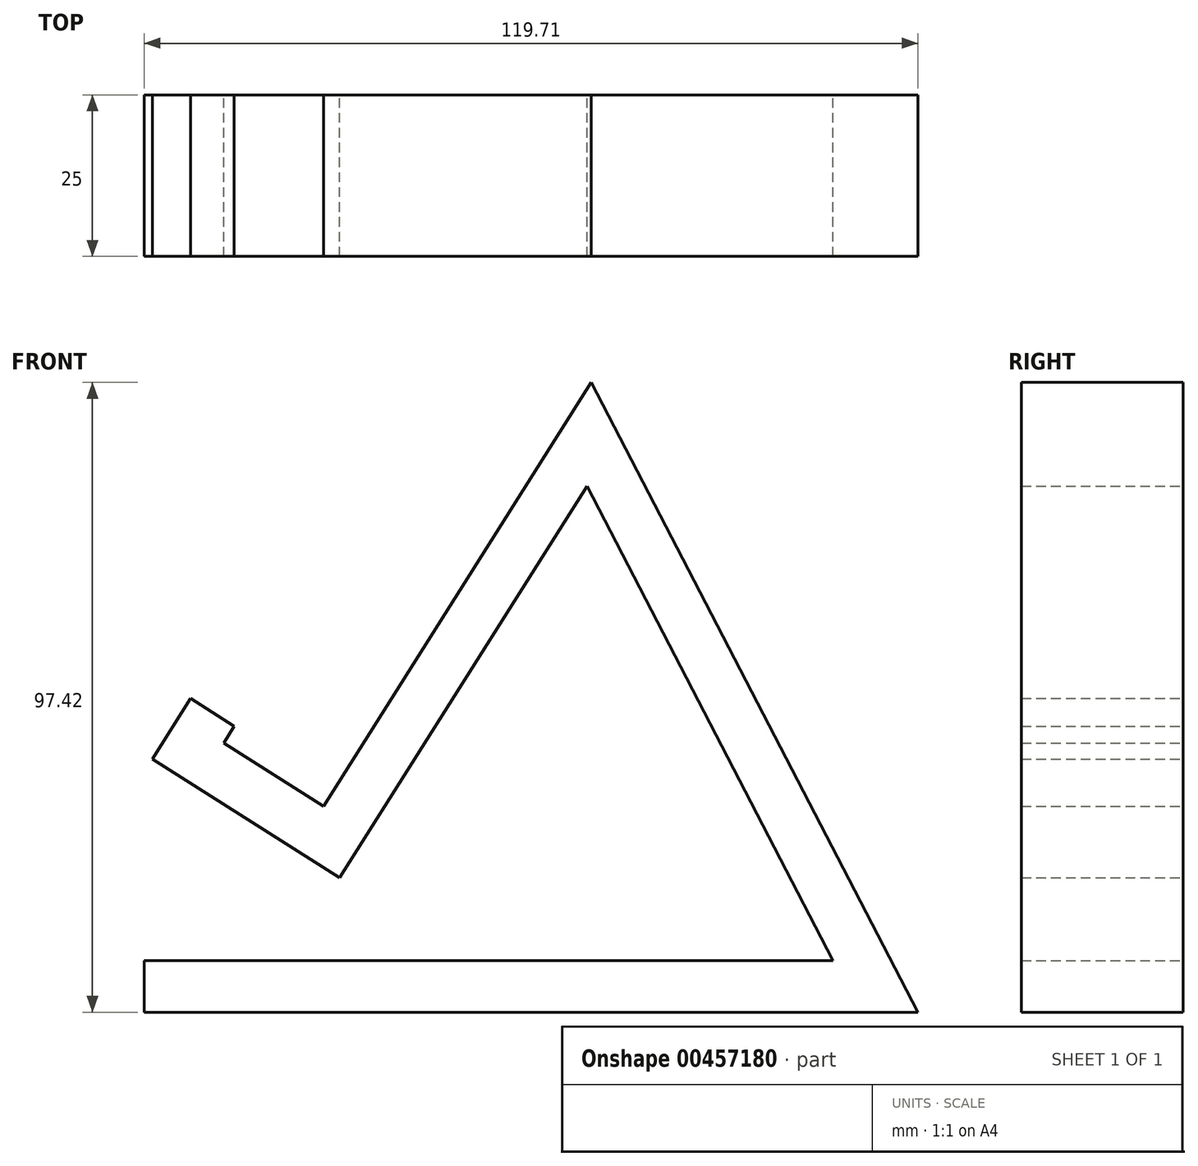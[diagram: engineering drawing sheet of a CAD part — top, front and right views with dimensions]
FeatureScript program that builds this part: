
annotation { "Feature Type Name" : "Feature", "Feature Type Description" : "" }
export const myFeature = defineFeature(function(context is Context, id is Id, definition is map)
    precondition{}
    {
        {
            var Q0;
            Q0=qCreatedBy(makeId("Front.planeOp"),FACE);
            var sketch = newSketch(context, id + "F0", { "sketchPlane" : qUnion([Q0])});
            skLineSegment(sketch, "E0", {"start": v(64.18, -45.98) * mm, "end": v(13.66, 51.44) * mm});
            skLineSegment(sketch, "E1", {"start": v(13.66, 51.44) * mm, "end": v(-27.77, -14.11) * mm});
            skLineSegment(sketch, "E2", {"start": v(-27.77, -14.11) * mm, "end": v(-43.23, -4.34) * mm});
            skLineSegment(sketch, "E3.1", {"start": v(-25.28, -25.15) * mm, "end": v(-54.27, -6.83) * mm});
            skLineSegment(sketch, "E4.0", {"start": v(51.02, -37.98) * mm, "end": v(12.97, 35.38) * mm});
            skLineSegment(sketch, "E5.0", {"start": v(12.97, 35.38) * mm, "end": v(-25.28, -25.15) * mm});
            skLineSegment(sketch, "E6", {"start": v(64.18, -45.98) * mm, "end": v(-55.53, -45.98) * mm});
            skLineSegment(sketch, "E7.0", {"start": v(51.02, -37.98) * mm, "end": v(-55.53, -37.98) * mm});
            skLineSegment(sketch, "E8", {"start": v(-55.53, -37.98) * mm, "end": v(-55.53, -45.98) * mm});
            skLineSegment(sketch, "E9", {"start": v(-43.23, -4.34) * mm, "end": v(-41.58, -1.72) * mm});
            skLineSegment(sketch, "E10.0", {"start": v(-50, -0.07) * mm, "end": v(-48.34, 2.55) * mm});
            skLineSegment(sketch, "E11", {"start": v(-50, -0.07) * mm, "end": v(-54.27, -6.83) * mm});
            skLineSegment(sketch, "E12", {"start": v(-48.34, 2.55) * mm, "end": v(-41.58, -1.72) * mm});
            skSolve(sketch);
        }
        {
            var Q0;
            Q0=makeQuery(id+"F0.imprint","IMPRINT",FACE,{"disambiguationData":[TD([[makeQuery(id+"F0.imprint","IMPRINT",EDGE,{"derivedFrom":sQuery(id+"F0.wireOp",EDGE,"E0")}),1.0]])]});
            extrude(context, id + "F1", {"entities" : qUnion([Q0]), "depth" : 25 * mm});
        }
    });
